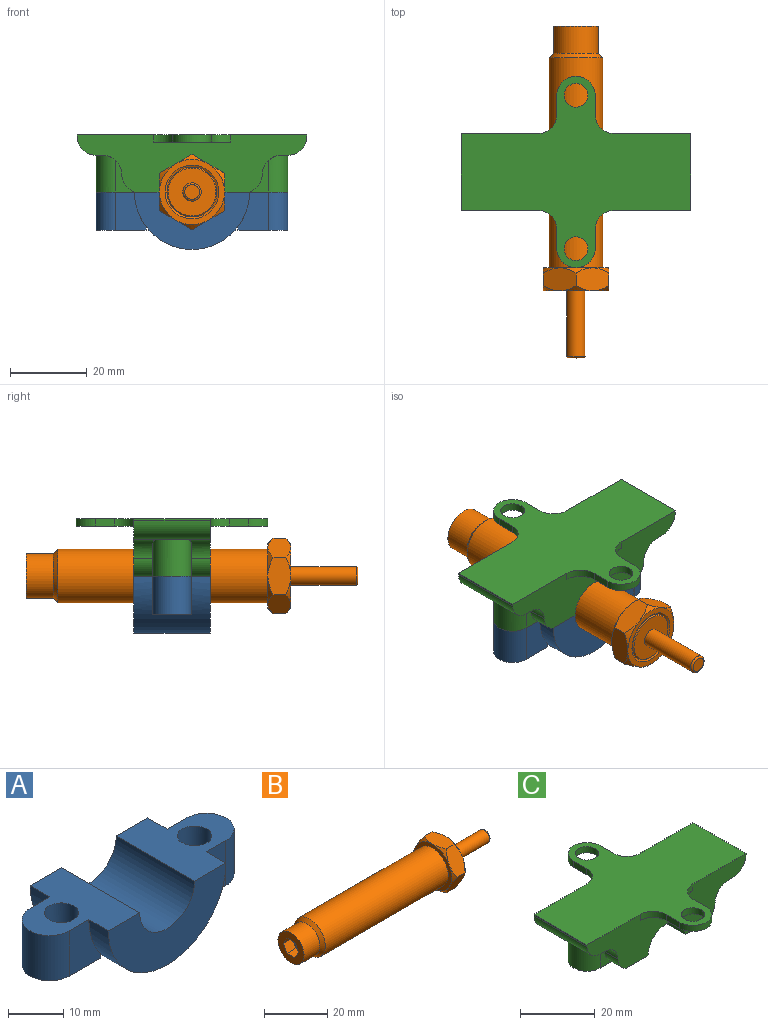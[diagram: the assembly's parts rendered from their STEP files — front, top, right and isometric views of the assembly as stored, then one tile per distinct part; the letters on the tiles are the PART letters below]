
ASSEMBLY  parts=3 mates=2
PART A: 18 faces, bbox 50x20x15 mm
  f0: plane 10x1mm, normal (1,0,0), area 10mm2, adj f5,f8,f9,f13
  f1: plane 10x1mm, normal (-1,0,0), area 10mm2, adj f3,f11,f12,f13
  f2: cylinder r=3.1mm len=10mm, axis (0,0,-1), area 194.8mm2, adj f3,f17
  f3: plane 13x10mm, normal (0,0,-1), area 89.1mm2, adj f1,f2,f10,f11,f12
  f4: cylinder r=3.1mm len=10mm, axis (0,0,-1), area 194.8mm2, adj f5,f16
  f5: plane 13x10mm, normal (0,0,-1), area 89.1mm2, adj f0,f4,f7,f8,f9
  f6: cylinder r=7mm len=20mm, axis (0,-1,0), area 439.8mm2, adj f14,f15,f16,f17
  f7: cylinder r=5mm len=10mm, axis (0,0,1), area 157.1mm2, adj f5,f8,f9,f16
  f8: plane 10x8mm, normal (0,1,0), area 61.6mm2, adj f0,f5,f7,f13,f16
  f9: plane 10x8mm, normal (0,-1,0), area 61.6mm2, adj f0,f5,f7,f13,f16
  f10: cylinder r=5mm len=10mm, axis (0,0,1), area 157.1mm2, adj f3,f11,f12,f17
  f11: plane 10x8mm, normal (0,-1,0), area 61.6mm2, adj f1,f3,f10,f13,f17
  f12: plane 10x8mm, normal (0,1,0), area 61.6mm2, adj f1,f3,f10,f13,f17
  f13: cylinder r=15mm len=30mm, axis (0,-1,0), area 749.4mm2, adj f0,f1,f8,f9,f11,f12,f14,f15
  f14: plane 30x15mm, normal (0,-1,0), area 276.5mm2, adj f6,f13,f16,f17
  f15: plane 30x15mm, normal (0,1,0), area 276.5mm2, adj f6,f13,f16,f17
  f16: plane 20x18mm, normal (0,0,1), area 219.1mm2, adj f4,f6,f7,f8,f9,f13,f14,f15
  f17: plane 20x18mm, normal (0,0,1), area 219.1mm2, adj f2,f6,f10,f11,f12,f13,f14,f15
PART B: 37 faces, bbox 86.6x19.6x19.6 mm
  f0: cone r=6.5mm half-angle=60deg, axis (1,0,0), area 23.3mm2, adj f6,f35
  f1: cylinder r=5.8mm len=11.6mm, axis (1,0,0), area 258.7mm2, adj f2,f15
  f2: cone r=6.4mm half-angle=45deg, axis (1,0,0), area 68.2mm2, adj f1,f3
  f3: cylinder r=7mm len=54.8mm, axis (1,0,0), area 2410.2mm2, adj f2,f36
  f4: cylinder r=2.4mm len=17.02mm, axis (1,0,0), area 256.7mm2, adj f5,f16
  f5: torus R=1.92mm, axis (-1,0,0), area 10.5mm2, adj f4,f7
  f6: cone r=6.62mm half-angle=45deg, axis (-1,0,0), area 15.6mm2, adj f0,f16
  f7: plane 3.84x3.84mm, normal (1,0,0), area 11.6mm2, adj f5
  f8: plane 4x3.46mm, normal (0,0,-1), area 13.9mm2, adj f9,f13,f14,f15
  f9: plane 4x3mm, normal (0,0.87,-0.5), area 13.9mm2, adj f8,f10,f14,f15
  f10: plane 4x3mm, normal (0,0.87,0.5), area 13.9mm2, adj f9,f11,f14,f15
  f11: plane 4x3.46mm, normal (0,0,1), area 13.9mm2, adj f10,f12,f14,f15
  f12: plane 4x3mm, normal (0,-0.87,0.5), area 13.9mm2, adj f11,f13,f14,f15
  f13: plane 4x3mm, normal (0,-0.87,-0.5), area 13.9mm2, adj f8,f12,f14,f15
  f14: plane 6.93x6mm, normal (-1,0,0), area 31.2mm2, adj f8,f9,f10,f11,f12,f13
  f15: plane 11.6x11.6mm, normal (-1,0,0), area 74.5mm2, adj f1,f8,f9,f10,f11,f12,f13
  f16: plane 12.5x12.5mm, normal (1,0,0), area 104.6mm2, adj f4,f6
  f17: cone r=9.16mm half-angle=45deg, axis (1,0,0), area 5.5mm2, adj f25,f34,f36
  f18: cone r=9.16mm half-angle=45deg, axis (1,0,0), area 5.5mm2, adj f33,f34,f36
  f19: cone r=9.16mm half-angle=45deg, axis (1,0,0), area 5.5mm2, adj f24,f25,f36
  f20: cone r=9.16mm half-angle=45deg, axis (1,0,0), area 5.5mm2, adj f32,f33,f36
  f21: cone r=9.16mm half-angle=45deg, axis (1,0,0), area 5.5mm2, adj f23,f24,f36
  f22: cone r=9.16mm half-angle=45deg, axis (1,0,0), area 5.5mm2, adj f23,f32,f36
  f23: plane 8.5x6mm, normal (0,-0.87,0.5), area 50mm2, adj f21,f22,f24,f30,f31,f32
  f24: plane 8.5x6mm, normal (0,-0.87,-0.5), area 50mm2, adj f19,f21,f23,f25,f29,f31
  f25: plane 9.82x6mm, normal (0,0,-1), area 50mm2, adj f17,f19,f24,f27,f29,f34
  f26: cone r=9.16mm half-angle=45deg, axis (-1,0,0), area 5.5mm2, adj f33,f34,f35
  f27: cone r=9.16mm half-angle=45deg, axis (-1,0,0), area 5.5mm2, adj f25,f34,f35
  f28: cone r=9.16mm half-angle=45deg, axis (-1,0,0), area 5.5mm2, adj f32,f33,f35
  f29: cone r=9.16mm half-angle=45deg, axis (-1,0,0), area 5.5mm2, adj f24,f25,f35
  f30: cone r=9.16mm half-angle=45deg, axis (-1,0,0), area 5.5mm2, adj f23,f32,f35
  f31: cone r=9.16mm half-angle=45deg, axis (-1,0,0), area 5.5mm2, adj f23,f24,f35
  f32: plane 9.82x6mm, normal (0,0,1), area 50mm2, adj f20,f22,f23,f28,f30,f33
  f33: plane 8.5x6mm, normal (0,0.87,0.5), area 50mm2, adj f18,f20,f26,f28,f32,f34
  f34: plane 8.5x6mm, normal (0,0.87,-0.5), area 50mm2, adj f17,f18,f25,f26,f27,f33
  f35: plane 17x17mm, normal (1,0,0), area 73mm2, adj f0,f26,f27,f28,f29,f30,f31
  f36: plane 17x17mm, normal (-1,0,0), area 73mm2, adj f3,f17,f18,f19,f20,f21,f22
PART C: 46 faces, bbox 60x50x15 mm
  f0: cylinder r=5mm len=6.28mm, axis (0,-1,0), area 40.3mm2, adj f1,f2,f6,f36,f38
  f1: plane 10x1.66mm, normal (0,0,-1), area 12.3mm2, adj f0,f6,f31,f38
  f2: cylinder r=5mm len=5mm, axis (0,-1,0), area 30.5mm2, adj f0,f6,f36,f41
  f3: plane 10x1.66mm, normal (0,0,-1), area 12.3mm2, adj f4,f10,f26,f39
  f4: cylinder r=5mm len=6.28mm, axis (0,-1,0), area 40.3mm2, adj f3,f5,f10,f34,f39
  f5: cylinder r=5mm len=5mm, axis (0,-1,0), area 30.5mm2, adj f4,f10,f34,f40
  f6: plane 60x15mm, normal (0,1,0), area 551.2mm2, adj f0,f1,f2,f7,f8,f9,f11,f15
  f7: plane 20x0.42mm, normal (1,0,0), area 8.5mm2, adj f6,f8,f10,f31
  f8: plane 60x50mm, normal (0,0,1), area 1439.6mm2, adj f6,f7,f9,f10,f12,f13,f14,f16
  f9: plane 20x0.42mm, normal (-1,0,0), area 8.5mm2, adj f6,f8,f10,f26
  f10: plane 60x15mm, normal (0,-1,0), area 551.2mm2, adj f3,f4,f5,f7,f8,f9,f11,f19
  f11: cylinder r=7mm len=20mm, axis (0,-1,0), area 439.8mm2, adj f6,f10,f40,f41
  f12: plane 5x2mm, normal (-1,0,0), area 10mm2, adj f8,f14,f15,f23
  f13: plane 5x2mm, normal (1,0,0), area 10mm2, adj f8,f14,f15,f22
  f14: cylinder r=5mm len=10mm, axis (0,0,1), area 31.4mm2, adj f8,f12,f13,f15
  f15: plane 20x15mm, normal (0,0,-1), area 119.8mm2, adj f6,f12,f13,f14,f22,f23,f24
  f16: plane 5x2mm, normal (1,0,0), area 10mm2, adj f8,f18,f19,f20
  f17: plane 5x2mm, normal (-1,0,0), area 10mm2, adj f8,f18,f19,f21
  f18: cylinder r=5mm len=10mm, axis (0,0,1), area 31.4mm2, adj f8,f16,f17,f19
  f19: plane 20x15mm, normal (0,0,-1), area 119.8mm2, adj f10,f16,f17,f18,f20,f21,f25
  f20: cylinder r=5mm len=5mm, axis (0,0,1), area 15.7mm2, adj f8,f10,f16,f19
  f21: cylinder r=5mm len=5mm, axis (0,0,-1), area 15.7mm2, adj f8,f10,f17,f19
  f22: cylinder r=5mm len=5mm, axis (0,0,1), area 15.7mm2, adj f6,f8,f13,f15
  f23: cylinder r=5mm len=5mm, axis (0,0,-1), area 15.7mm2, adj f6,f8,f12,f15
  f24: cylinder r=3.1mm len=6.2mm, axis (0,0,1), area 39mm2, adj f8,f15
  f25: cylinder r=3.1mm len=6.2mm, axis (0,0,1), area 39mm2, adj f8,f19
  f26: cylinder r=5mm len=20mm, axis (0,-1,0), area 157.1mm2, adj f3,f6,f9,f10,f27
  f27: plane 10x1.66mm, normal (0,0,-1), area 12.3mm2, adj f6,f26,f28,f39
  f28: cylinder r=5mm len=6.28mm, axis (0,-1,0), area 40.3mm2, adj f6,f27,f32,f35,f39
  f29: cylinder r=5mm len=6.28mm, axis (0,-1,0), area 40.3mm2, adj f10,f30,f33,f37,f38
  f30: plane 10x1.66mm, normal (0,0,-1), area 12.3mm2, adj f10,f29,f31,f38
  f31: cylinder r=5mm len=20mm, axis (0,-1,0), area 157.1mm2, adj f1,f6,f7,f10,f30
  f32: cylinder r=5mm len=5mm, axis (0,-1,0), area 30.5mm2, adj f6,f28,f35,f40
  f33: cylinder r=5mm len=5mm, axis (0,-1,0), area 30.5mm2, adj f10,f29,f37,f41
  f34: plane 8.3x5mm, normal (0,-1,0), area 16.1mm2, adj f4,f5,f39,f40
  f35: plane 8.3x5mm, normal (0,1,0), area 16.1mm2, adj f28,f32,f39,f40
  f36: plane 8.3x5mm, normal (0,1,0), area 16.1mm2, adj f0,f2,f38,f41
  f37: plane 8.3x5mm, normal (0,-1,0), area 16.1mm2, adj f29,f33,f38,f41
  f38: cylinder r=5mm len=10mm, axis (0,0,1), area 147.7mm2, adj f0,f1,f29,f30,f36,f37,f41
  f39: cylinder r=5mm len=10mm, axis (0,0,1), area 147.7mm2, adj f3,f4,f27,f28,f34,f35,f40
  f40: plane 20x18mm, normal (0,0,-1), area 219.1mm2, adj f5,f6,f10,f11,f32,f34,f35,f39
  f41: plane 20x18mm, normal (0,0,-1), area 219.1mm2, adj f2,f6,f10,f11,f33,f36,f37,f38
  f42: cone r=0mm half-angle=59deg, axis (0,0,-1), area 35.2mm2, adj f43
  f43: cylinder r=3.1mm len=10mm, axis (0,0,-1), area 194.8mm2, adj f41,f42
  f44: cone r=0mm half-angle=59deg, axis (0,0,-1), area 35.2mm2, adj f45
  f45: cylinder r=3.1mm len=10mm, axis (0,0,-1), area 194.8mm2, adj f40,f44
PLACE A t=(-11.42,14.27,8.8)mm
PLACE B rot(axis=(-0.58,0.58,-0.58),120deg) t=(-11.42,-26.73,8.8)mm
PLACE C t=(-11.42,14.27,8.8)mm
MATE fastened B.f0 <-> C.f11  axis (0,1,0) through (-11.42,-20.73,8.8)mm
MATE fastened A.f4 <-> C.f44  axis (0,0,1) through (-28.42,4.27,8.8)mm
